# Revit family: test_3types
name_source: partatom
category: Lighting Fixtures
revit_build: Autodesk Revit 2018 (Build: 20181011_1500(x64)
units: mm (PartAtom-declared; Revit-internal decimal feet)

## family parameters
Cut with Voids When Loaded = No
Host = Face
Light Source = No
OmniClass Number = 23.80.70.11
OmniClass Title = Luminaries for Internal Lighting
Part Type = Normal
Room Calculation Point = No
Round Connector Dimension = Use Diameter
Shared = Yes

## types (1)
- This Family uses a Type Catalog
    Apparent Load = 10 VA
    CRI = 80
    Color = white
    Colour temperature (K) = 6500
    Connection Load = 10 VA
    Default Elevation = 0 mm  [stored 0 ft]
    Degree of protection = IP20
    Dimming/Balast = - / E
    Lamp = Lamp
    Lamp_0 = Lamp
    Light Source = TestLS : Typ 1
    Luminous flux of luminaire (lm) = 1000
    Mat = TRILUX_RAL9016
    SEO = TRILUX_WH_2700
    Safety class = I
    TK = 00000000
    TOC = 0000000
    Weight = 6.1
    h = 100 mm  [stored 0.328084 ft]
    l = 400 mm  [stored 1.31234 ft]
    w = 400 mm  [stored 1.31234 ft]

note: [stored X ft] marks values corroborated as IEEE doubles in the binary element streams (Revit-internal decimal feet)

## geometry (parser evidence)
native form markers: Sweep x5
no freeform markers — native parametric forms only
